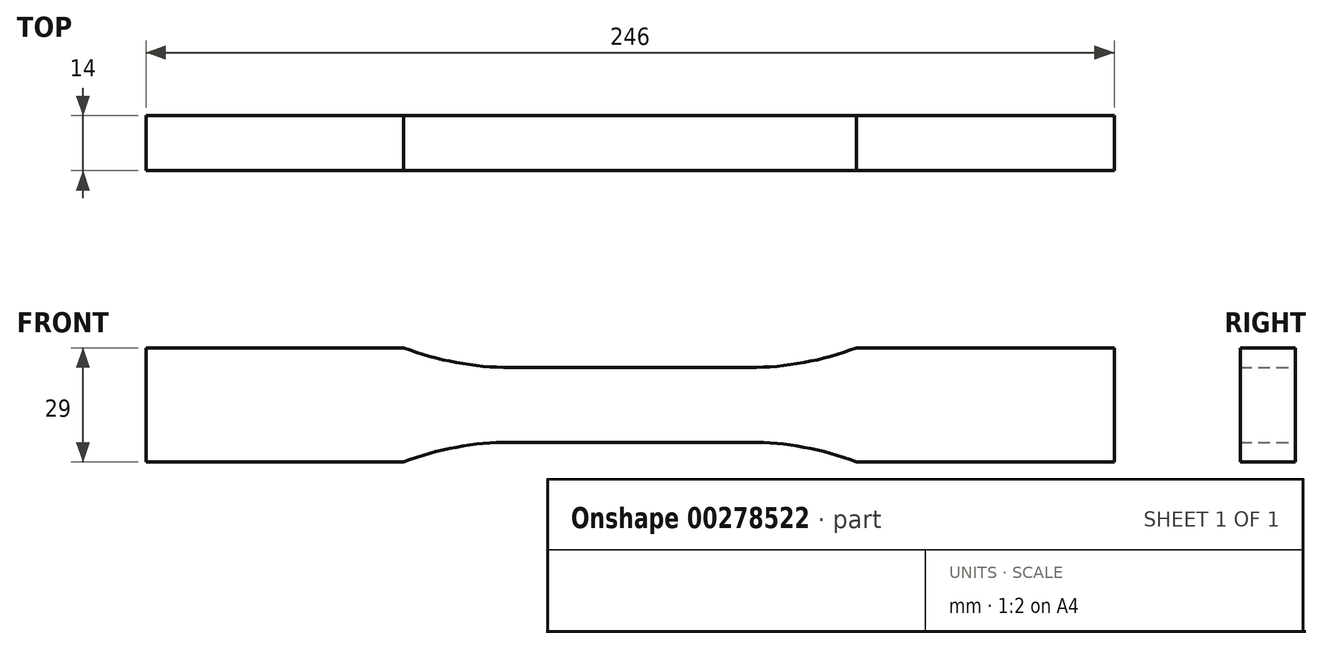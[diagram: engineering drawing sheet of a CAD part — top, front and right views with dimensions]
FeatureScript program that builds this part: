
annotation { "Feature Type Name" : "Feature", "Feature Type Description" : "" }
export const myFeature = defineFeature(function(context is Context, id is Id, definition is map)
    precondition{}
    {
        {
            var Q0;
            Q0=qCreatedBy(makeId("Front.planeOp"),FACE);
            var sketch = newSketch(context, id + "F0", { "sketchPlane" : qUnion([Q0])});
            skLineSegment(sketch, "E0", {"start": v(0, 9.5) * mm, "end": v(30.39, 9.5) * mm});
            skArc(sketch, "E1", {"start": v(30.39, 9.5) * mm, "mid": v(44.17, 10.76) * mm, "end": v(57.5, 14.5) * mm});
            skLineSegment(sketch, "E2", {"start": v(57.5, 14.5) * mm, "end": v(123, 14.5) * mm});
            skLineSegment(sketch, "E3.MirrorCS", {"start": v(57.5, -14.5) * mm, "end": v(123, -14.5) * mm});
            skLineSegment(sketch, "E4.MirrorCS", {"start": v(0, -9.5) * mm, "end": v(30.39, -9.5) * mm});
            skArc(sketch, "E5.MirrorCS", {"start": v(30.39, -9.5) * mm, "mid": v(44.17, -10.76) * mm, "end": v(57.5, -14.5) * mm});
            skLineSegment(sketch, "E6.MirrorCS", {"start": v(0, 9.5) * mm, "end": v(-30.39, 9.5) * mm});
            skArc(sketch, "E7.MirrorCS", {"start": v(-30.39, 9.5) * mm, "mid": v(-44.17, 10.76) * mm, "end": v(-57.5, 14.5) * mm});
            skLineSegment(sketch, "E8.MirrorCS", {"start": v(-57.5, 14.5) * mm, "end": v(-123, 14.5) * mm});
            skLineSegment(sketch, "E9.MirrorCS", {"start": v(-57.5, -14.5) * mm, "end": v(-123, -14.5) * mm});
            skArc(sketch, "E10.MirrorCS", {"start": v(-30.39, -9.5) * mm, "mid": v(-44.17, -10.76) * mm, "end": v(-57.5, -14.5) * mm});
            skLineSegment(sketch, "E11.MirrorCS", {"start": v(0, -9.5) * mm, "end": v(-30.39, -9.5) * mm});
            skLineSegment(sketch, "E12", {"start": v(-123, 14.5) * mm, "end": v(-123, -14.5) * mm});
            skLineSegment(sketch, "E13", {"start": v(123, 14.5) * mm, "end": v(123, -14.5) * mm});
            skSolve(sketch);
        }
        {
            var Q0;
            Q0=makeQuery(id+"F0.imprint","IMPRINT",FACE,{"disambiguationData":[TD([[makeQuery(id+"F0.imprint","IMPRINT",EDGE,{"derivedFrom":sQuery(id+"F0.wireOp",EDGE,"E1")}),-1.0]])]});
            extrude(context, id + "F1", {"entities" : qUnion([Q0]), "endBound" : BoundingType.SYMMETRIC, "depth" : 14 * mm});
        }
    });
